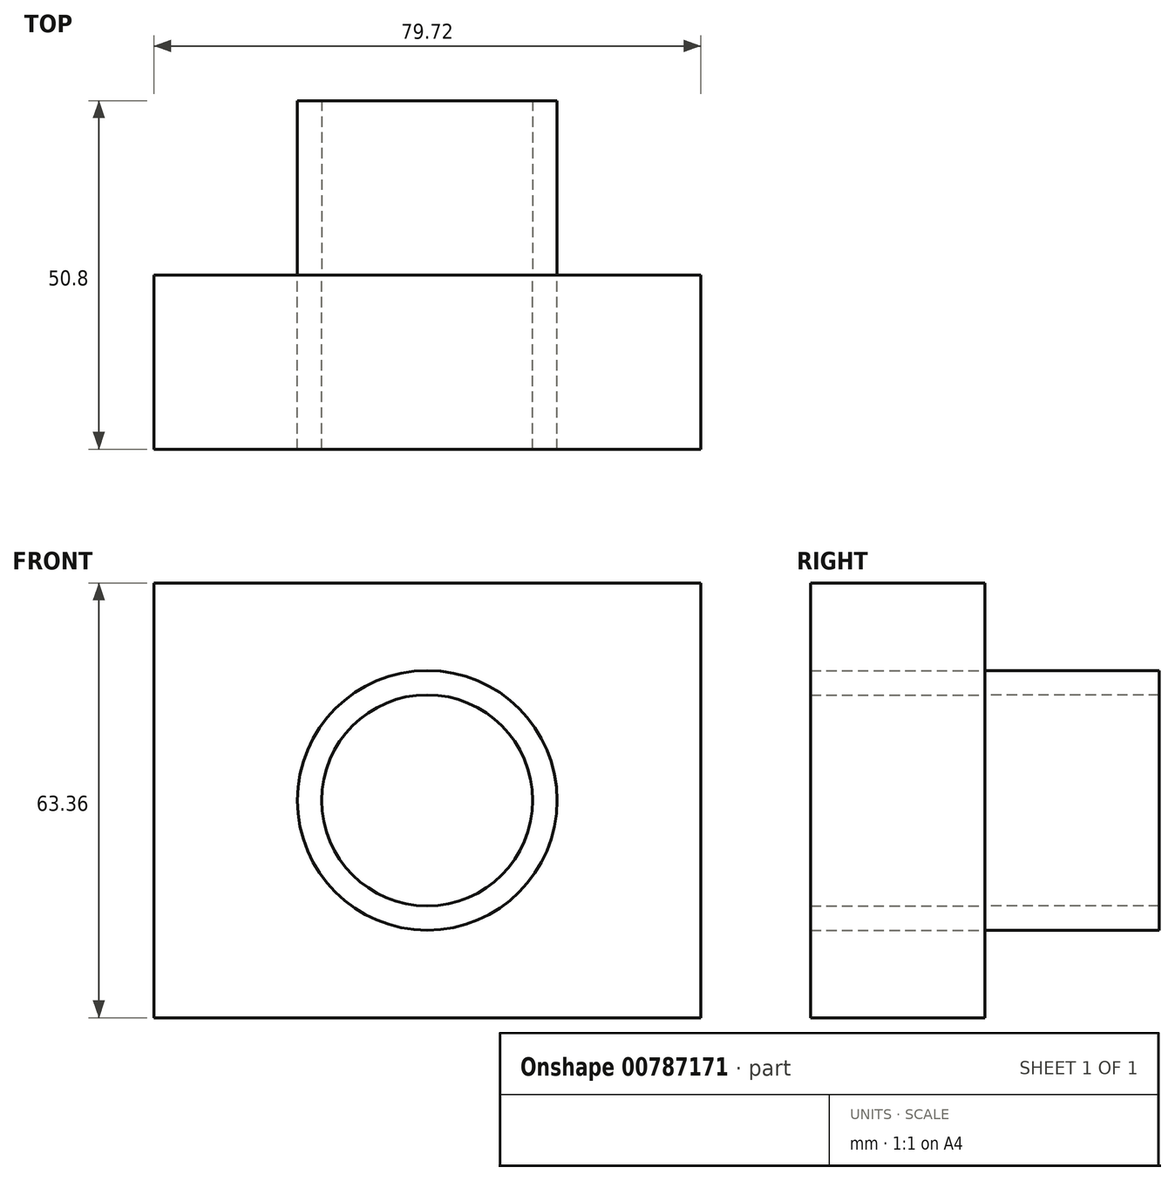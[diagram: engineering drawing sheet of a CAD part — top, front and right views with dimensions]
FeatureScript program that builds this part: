
annotation { "Feature Type Name" : "Feature", "Feature Type Description" : "" }
export const myFeature = defineFeature(function(context is Context, id is Id, definition is map)
    precondition{}
    {
        {
            var Q0;
            Q0=qCreatedBy(makeId("Front.planeOp"),FACE);
            var sketch = newSketch(context, id + "F0", { "sketchPlane" : qUnion([Q0])});
            skLineSegment(sketch, "E0.bottom", {"start": v(39.86, 31.68) * mm, "end": v(-39.86, 31.68) * mm});
            skLineSegment(sketch, "E0.top", {"start": v(39.86, -31.68) * mm, "end": v(-39.86, -31.68) * mm});
            skLineSegment(sketch, "E0.left", {"start": v(39.86, 31.68) * mm, "end": v(39.86, -31.68) * mm});
            skLineSegment(sketch, "E0.right", {"start": v(-39.86, 31.68) * mm, "end": v(-39.86, -31.68) * mm});
            skPoint(sketch, "E0.middle", {"position": v(0, 0) * mm});
            skCircle(sketch, "E1", {"center": v(0, 0) * mm, "radius": 18.93 * mm});
            skCircle(sketch, "E2", {"center": v(0, 0) * mm, "radius": 15.38 * mm});
            skSolve(sketch);
        }
        {
            var Q0;
            Q0 = qSketchRegion(id + "F0", true);
            extrude(context, id + "F1", {"entities" : qUnion([Q0]), "depth" : 25.4 * mm, "offsetDistance" : 25.4 * mm});
        }
        {
            var Q0;
            Q0=makeQuery(id+"F0.imprint","IMPRINT",FACE,{"disambiguationData":[TD([[makeQuery(id+"F0.imprint","IMPRINT",EDGE,{"derivedFrom":sQuery(id+"F0.wireOp",EDGE,"E1")}),1.0]])]});
            extrude(context, id + "F2", {"entities" : qUnion([Q0]), "operationType" : NewBodyOperationType.ADD, "oppositeDirection" : true, "depth" : 25.4 * mm, "offsetDistance" : 25.4 * mm});
        }
        {
            var Q0;
            Q0=makeQuery(id+"F2.opExtrude","CAP_FACE",FACE,{"disambiguationData":[OSD([sQuery(id+"F0.wireOp",EDGE,"E1"),sQuery(id+"F0.wireOp",EDGE,"E2")])],"isStart":true});
            extrude(context, id + "F3", {"entities" : qUnion([Q0]), "depth" : 25.4 * mm, "offsetDistance" : 25.4 * mm});
        }
    });
